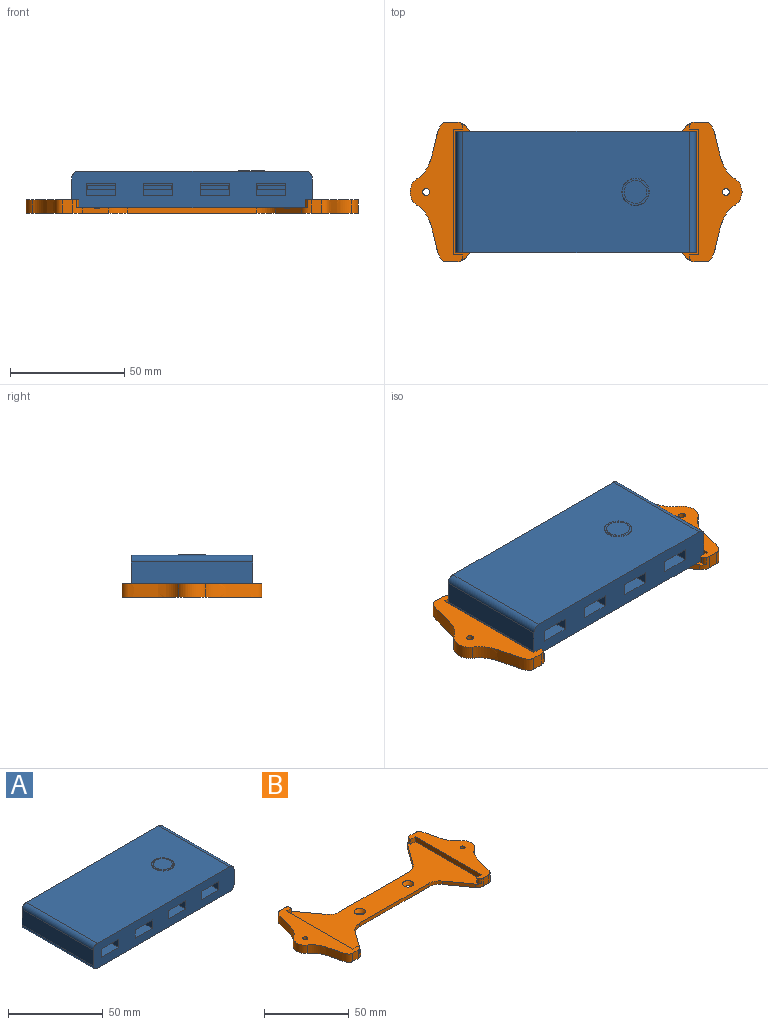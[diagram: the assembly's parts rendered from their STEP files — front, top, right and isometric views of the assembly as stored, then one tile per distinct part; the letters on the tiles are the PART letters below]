
ASSEMBLY  parts=2 mates=1
PART A: 89 faces, bbox 105x53x16.5 mm
  f0: plane 105x16mm, normal (0,1,0), area 1523.6mm2, adj f2,f3,f4,f5,f6,f7,f8,f9
  f1: plane 105x16mm, normal (0,-1,0), area 1399.4mm2, adj f2,f3,f4,f5,f6,f7,f8,f9
  f2: plane 53x10mm, normal (1,0,0), area 530mm2, adj f0,f1,f7,f9
  f3: plane 53x10mm, normal (-1,0,0), area 530mm2, adj f0,f1,f6,f8
  f4: plane 99x53mm, normal (0,0,1), area 5133.9mm2, adj f0,f1,f8,f9,f13
  f5: plane 99x53mm, normal (0,0,-1), area 5093.1mm2, adj f0,f1,f6,f7,f81,f83,f85,f87
  f6: cylinder r=3mm len=53mm, axis (0,-1,0), area 249.8mm2, adj f0,f1,f3,f5
  f7: cylinder r=3mm len=53mm, axis (0,1,0), area 249.8mm2, adj f0,f1,f2,f5
  f8: cylinder r=3mm len=53mm, axis (0,1,0), area 249.8mm2, adj f0,f1,f3,f4
  f9: cylinder r=3mm len=53mm, axis (0,-1,0), area 249.8mm2, adj f0,f1,f2,f4
  f10: plane 11.6x11.6mm, normal (0,0,1), area 27.1mm2, adj f11,f13
  f11: cylinder r=5mm len=10mm, axis (0,0,-1), area 1.6mm2, adj f10,f12
  f12: plane 10x10mm, normal (0,0,1), area 78.5mm2, adj f11
  f13: cone r=5.8mm half-angle=45deg, axis (0,0,-1), area 10.5mm2, adj f4,f10
  f14: plane 10x5.35mm, normal (-1,0,0), area 53.5mm2, adj f1,f15,f17,f49
  f15: plane 12.75x10mm, normal (0,0,-1), area 127.5mm2, adj f1,f14,f16,f49
  f16: plane 10x5.35mm, normal (1,0,0), area 53.5mm2, adj f1,f15,f17,f49
  f17: plane 12.75x10mm, normal (0,0,1), area 127.5mm2, adj f1,f14,f16,f49
  f18: plane 10x5.35mm, normal (-1,0,0), area 53.5mm2, adj f1,f19,f21,f44
  f19: plane 12.75x10mm, normal (0,0,-1), area 127.5mm2, adj f1,f18,f20,f44
  f20: plane 10x5.35mm, normal (1,0,0), area 53.5mm2, adj f1,f19,f21,f44
  f21: plane 12.75x10mm, normal (0,0,1), area 127.5mm2, adj f1,f18,f20,f44
  f22: plane 10x5.35mm, normal (-1,0,0), area 53.5mm2, adj f1,f23,f25,f39
  f23: plane 12.75x10mm, normal (0,0,-1), area 127.5mm2, adj f1,f22,f24,f39
  f24: plane 10x5.35mm, normal (1,0,0), area 53.5mm2, adj f1,f23,f25,f39
  f25: plane 12.75x10mm, normal (0,0,1), area 127.5mm2, adj f1,f22,f24,f39
  f26: plane 10x5.35mm, normal (-1,0,0), area 53.5mm2, adj f1,f27,f29,f34
  f27: plane 12.75x10mm, normal (0,0,-1), area 127.5mm2, adj f1,f26,f28,f34
  f28: plane 10x5.35mm, normal (1,0,0), area 53.5mm2, adj f1,f27,f29,f34
  f29: plane 12.75x10mm, normal (0,0,1), area 127.5mm2, adj f1,f26,f28,f34
  f30: plane 7.25x1.75mm, normal (-1,0,0), area 12.7mm2, adj f31,f33,f34,f50
  f31: plane 12.25x7.25mm, normal (0,0,1), area 88.8mm2, adj f30,f32,f34,f50
  f32: plane 7.25x1.75mm, normal (1,0,0), area 12.7mm2, adj f31,f33,f34,f50
  f33: plane 12.25x7.25mm, normal (0,0,-1), area 88.8mm2, adj f30,f32,f34,f50
  f34: plane 12.75x5.35mm, normal (0,-1,0), area 46.8mm2, adj f26,f27,f28,f29,f30,f31,f32,f33
  f35: plane 12.25x7.25mm, normal (0,0,-1), area 88.8mm2, adj f36,f38,f39,f51
  f36: plane 7.25x1.75mm, normal (-1,0,0), area 12.7mm2, adj f35,f37,f39,f51
  f37: plane 12.25x7.25mm, normal (0,0,1), area 88.8mm2, adj f36,f38,f39,f51
  f38: plane 7.25x1.75mm, normal (1,0,0), area 12.7mm2, adj f35,f37,f39,f51
  f39: plane 12.75x5.35mm, normal (0,-1,0), area 46.8mm2, adj f22,f23,f24,f25,f35,f36,f37,f38
  f40: plane 12.25x7.25mm, normal (0,0,-1), area 88.8mm2, adj f41,f43,f44,f52
  f41: plane 7.25x1.75mm, normal (-1,0,0), area 12.7mm2, adj f40,f42,f44,f52
  f42: plane 12.25x7.25mm, normal (0,0,1), area 88.8mm2, adj f41,f43,f44,f52
  f43: plane 7.25x1.75mm, normal (1,0,0), area 12.7mm2, adj f40,f42,f44,f52
  f44: plane 12.75x5.35mm, normal (0,-1,0), area 46.8mm2, adj f18,f19,f20,f21,f40,f41,f42,f43
  f45: plane 12.25x7.25mm, normal (0,0,-1), area 88.8mm2, adj f46,f48,f49,f53
  f46: plane 7.25x1.75mm, normal (-1,0,0), area 12.7mm2, adj f45,f47,f49,f53
  f47: plane 12.25x7.25mm, normal (0,0,1), area 88.8mm2, adj f46,f48,f49,f53
  f48: plane 7.25x1.75mm, normal (1,0,0), area 12.7mm2, adj f45,f47,f49,f53
  f49: plane 12.75x5.35mm, normal (0,-1,0), area 46.8mm2, adj f14,f15,f16,f17,f45,f46,f47,f48
  f50: plane 12.25x1.75mm, normal (0,-1,0), area 21.4mm2, adj f30,f31,f32,f33
  f51: plane 12.25x1.75mm, normal (0,-1,0), area 21.4mm2, adj f35,f36,f37,f38
  f52: plane 12.25x1.75mm, normal (0,-1,0), area 21.4mm2, adj f40,f41,f42,f43
  f53: plane 12.25x1.75mm, normal (0,-1,0), area 21.4mm2, adj f45,f46,f47,f48
  f54: plane 12.75x10.25mm, normal (0,0,-1), area 130.7mm2, adj f0,f55,f57,f71
  f55: plane 10.25x5.35mm, normal (-1,0,0), area 54.8mm2, adj f0,f54,f56,f71
  f56: plane 12.75x10.25mm, normal (0,0,1), area 130.7mm2, adj f0,f55,f57,f71
  f57: plane 10.25x5.35mm, normal (1,0,0), area 54.8mm2, adj f0,f54,f56,f71
  f58: plane 10.25x5.35mm, normal (1,0,0), area 54.8mm2, adj f0,f59,f61,f66
  f59: plane 12.75x10.25mm, normal (0,0,-1), area 130.7mm2, adj f0,f58,f60,f66
  f60: plane 10.25x5.35mm, normal (-1,0,0), area 54.8mm2, adj f0,f59,f61,f66
  f61: plane 12.75x10.25mm, normal (0,0,1), area 130.7mm2, adj f0,f58,f60,f66
  f62: plane 7.75x1.75mm, normal (1,0,0), area 13.6mm2, adj f63,f65,f66,f72
  f63: plane 12.25x7.75mm, normal (0,0,1), area 94.9mm2, adj f62,f64,f66,f72
  f64: plane 7.75x1.75mm, normal (-1,0,0), area 13.6mm2, adj f63,f65,f66,f72
  f65: plane 12.25x7.75mm, normal (0,0,-1), area 94.9mm2, adj f62,f64,f66,f72
  f66: plane 12.75x5.35mm, normal (0,1,0), area 46.8mm2, adj f58,f59,f60,f61,f62,f63,f64,f65
  f67: plane 7.75x1.75mm, normal (1,0,0), area 13.6mm2, adj f68,f70,f71,f73
  f68: plane 12.25x7.75mm, normal (0,0,1), area 94.9mm2, adj f67,f69,f71,f73
  f69: plane 7.75x1.75mm, normal (-1,0,0), area 13.6mm2, adj f68,f70,f71,f73
  f70: plane 12.25x7.75mm, normal (0,0,-1), area 94.9mm2, adj f67,f69,f71,f73
  f71: plane 12.75x5.35mm, normal (0,1,0), area 46.8mm2, adj f54,f55,f56,f57,f67,f68,f69,f70
  f72: plane 12.25x1.75mm, normal (0,1,0), area 21.4mm2, adj f62,f63,f64,f65
  f73: plane 12.25x1.75mm, normal (0,1,0), area 21.4mm2, adj f67,f68,f69,f70
  f74: plane 6.9x4mm, normal (0,0,-1), area 27.6mm2, adj f0,f75,f79,f80
  f75: plane 4x1.1mm, normal (-1,0,0), area 4.4mm2, adj f0,f74,f76,f80
  f76: plane 4x0.75mm, normal (-0.73,0,0.68), area 4.1mm2, adj f0,f75,f77,f80
  f77: plane 5.5x4mm, normal (0,0,1), area 22mm2, adj f0,f76,f78,f80
  f78: plane 4x0.75mm, normal (0.73,0,0.68), area 4.1mm2, adj f0,f77,f79,f80
  f79: plane 4x1.1mm, normal (1,0,0), area 4.4mm2, adj f0,f74,f78,f80
  f80: plane 6.9x1.85mm, normal (0,1,0), area 12.2mm2, adj f74,f75,f76,f77,f78,f79
  f81: cylinder r=3.5mm len=7mm, axis (0,0,1), area 5.5mm2, adj f5,f82
  f82: plane 7x7mm, normal (0,0,-1), area 38.5mm2, adj f81
  f83: cylinder r=3.5mm len=7mm, axis (0,0,1), area 5.5mm2, adj f5,f84
  f84: plane 7x7mm, normal (0,0,-1), area 38.5mm2, adj f83
  f85: cylinder r=3.5mm len=7mm, axis (0,0,1), area 5.5mm2, adj f5,f86
  f86: plane 7x7mm, normal (0,0,-1), area 38.5mm2, adj f85
  f87: cylinder r=3.5mm len=7mm, axis (0,0,1), area 5.5mm2, adj f5,f88
  f88: plane 7x7mm, normal (0,0,-1), area 38.5mm2, adj f87
PART B: 60 faces, bbox 145x61x6 mm
  f0: plane 145x61mm, normal (0,0,-1), area 4109.9mm2, adj f2,f3,f8,f9,f10,f11,f12,f13
  f1: plane 107x60.55mm, normal (0,0,1), area 2740.6mm2, adj f5,f6,f16,f17,f18,f19,f20,f21
  f2: plane 6x4.44mm, normal (0,1,0), area 26.6mm2, adj f0,f7,f15,f56
  f3: plane 6x4.44mm, normal (0,-1,0), area 26.6mm2, adj f0,f7,f12,f59
  f4: plane 61x23mm, normal (0,0,1), area 678.7mm2, adj f5,f6,f8,f9,f10,f11,f14,f19
  f5: plane 4x3.5mm, normal (0,-1,0), area 14mm2, adj f1,f4,f19,f23
  f6: plane 4x3.5mm, normal (0,1,0), area 14mm2, adj f1,f4,f19,f21
  f7: plane 61x23mm, normal (0,0,1), area 678.7mm2, adj f2,f3,f12,f13,f15,f16,f17,f18
  f8: plane 6x4.44mm, normal (0,1,0), area 26.6mm2, adj f0,f4,f14,f57
  f9: plane 6x4.44mm, normal (0,-1,0), area 26.6mm2, adj f0,f4,f11,f58
  f10: cylinder r=7.07mm len=11.45mm, axis (0,0,1), area 80mm2, adj f0,f4,f11,f14
  f11: extruded ~24.78x13.08mm, area 176.1mm2, adj f0,f4,f9,f10
  f12: extruded ~24.78x13.08mm, area 176.1mm2, adj f0,f3,f7,f13
  f13: cylinder r=7.07mm len=11.45mm, axis (0,0,1), area 80mm2, adj f0,f7,f12,f15
  f14: extruded ~24.78x13.08mm, area 176.1mm2, adj f0,f4,f8,f10
  f15: extruded ~24.78x13.08mm, area 176.1mm2, adj f0,f2,f7,f13
  f16: plane 55x3.5mm, normal (1,0,0), area 192.5mm2, adj f1,f7,f17,f18
  f17: plane 4x3.5mm, normal (0,-1,0), area 14mm2, adj f1,f7,f16,f22
  f18: plane 4x3.5mm, normal (0,1,0), area 14mm2, adj f1,f7,f16,f20
  f19: plane 55x3.5mm, normal (-1,0,0), area 192.5mm2, adj f1,f4,f5,f6
  f20: plane 3.5x1mm, normal (1,0,0), area 3.5mm2, adj f1,f7,f18,f54
  f21: plane 3.5x1mm, normal (-1,0,0), area 3.5mm2, adj f1,f4,f6,f55
  f22: plane 3.5x1mm, normal (1,0,0), area 3.5mm2, adj f1,f7,f17,f52
  f23: plane 3.5x1mm, normal (-1,0,0), area 3.5mm2, adj f1,f4,f5,f53
  f24: plane 15.97x11.51mm, normal (0.81,0.58,0), area 49.2mm2, adj f0,f1,f26,f56
  f25: plane 15.97x11.51mm, normal (-0.81,0.58,0), area 49.2mm2, adj f0,f1,f28,f57
  f26: cylinder r=10mm len=8.11mm, axis (0,0,1), area 23.7mm2, adj f0,f1,f24,f27
  f27: plane 56.76x2.5mm, normal (0,1,0), area 141.9mm2, adj f0,f1,f26,f28
  f28: cylinder r=10mm len=8.11mm, axis (0,0,1), area 23.7mm2, adj f0,f1,f25,f27
  f29: plane 15.97x11.51mm, normal (-0.81,-0.58,0), area 49.2mm2, adj f0,f1,f31,f58
  f30: plane 15.97x11.51mm, normal (0.81,-0.58,0), area 49.2mm2, adj f0,f1,f33,f59
  f31: cylinder r=10mm len=8.11mm, axis (0,0,1), area 23.7mm2, adj f0,f1,f29,f32
  f32: plane 56.76x2.5mm, normal (0,-1,0), area 141.9mm2, adj f0,f1,f31,f33
  f33: cylinder r=10mm len=8.11mm, axis (0,0,1), area 23.7mm2, adj f0,f1,f30,f32
  f34: cone r=3.3mm half-angle=30deg, axis (0,0,1), area 46.8mm2, adj f0,f1
  f35: cone r=3.3mm half-angle=30deg, axis (0,0,1), area 46.8mm2, adj f0,f1
  f36: cylinder r=1.5mm len=3.25mm, axis (0,0,1), area 30.6mm2, adj f4,f51
  f37: cylinder r=1.5mm len=3.25mm, axis (0,0,1), area 30.6mm2, adj f7,f44
  f38: plane 2.75x2.53mm, normal (0.57,0.82,0), area 8.5mm2, adj f0,f39,f43,f44
  f39: plane 2.78x2.75mm, normal (-0.43,0.9,0), area 8.5mm2, adj f0,f38,f40,f44
  f40: plane 3.06x2.75mm, normal (-1,0.08,0), area 8.5mm2, adj f0,f39,f41,f44
  f41: plane 2.75x2.53mm, normal (-0.57,-0.82,0), area 8.5mm2, adj f0,f40,f42,f44
  f42: plane 2.78x2.75mm, normal (0.43,-0.9,0), area 8.5mm2, adj f0,f41,f43,f44
  f43: plane 3.06x2.75mm, normal (1,-0.08,0), area 8.5mm2, adj f0,f38,f42,f44
  f44: plane 6.13x5.56mm, normal (0,0,-1), area 17.5mm2, adj f37,f38,f39,f40,f41,f42,f43
  f45: plane 3.06x2.75mm, normal (1,0.08,0), area 8.5mm2, adj f0,f46,f50,f51
  f46: plane 2.78x2.75mm, normal (0.43,0.9,0), area 8.5mm2, adj f0,f45,f47,f51
  f47: plane 2.75x2.53mm, normal (-0.57,0.82,0), area 8.5mm2, adj f0,f46,f48,f51
  f48: plane 3.06x2.75mm, normal (-1,-0.08,0), area 8.5mm2, adj f0,f47,f49,f51
  f49: plane 2.78x2.75mm, normal (-0.43,-0.9,0), area 8.5mm2, adj f0,f48,f50,f51
  f50: plane 2.75x2.53mm, normal (0.57,-0.82,0), area 8.5mm2, adj f0,f45,f49,f51
  f51: plane 6.13x5.56mm, normal (0,0,-1), area 17.5mm2, adj f36,f45,f46,f47,f48,f49,f50
  f52: cylinder r=2mm len=3.5mm, axis (0,0,-1), area 7.7mm2, adj f1,f7,f22,f56
  f53: cylinder r=2mm len=3.5mm, axis (0,0,1), area 7.7mm2, adj f1,f4,f23,f57
  f54: cylinder r=2mm len=3.5mm, axis (0,0,1), area 7.7mm2, adj f1,f7,f20,f59
  f55: cylinder r=2mm len=3.5mm, axis (0,0,-1), area 7.7mm2, adj f1,f4,f21,f58
  f56: cylinder r=5mm len=6mm, axis (0,0,1), area 17.1mm2, adj f0,f1,f2,f7,f24,f52
  f57: cylinder r=5mm len=6mm, axis (0,0,1), area 17.1mm2, adj f0,f1,f4,f8,f25,f53
  f58: cylinder r=5mm len=6mm, axis (0,0,1), area 17.1mm2, adj f0,f1,f4,f9,f29,f55
  f59: cylinder r=5mm len=6mm, axis (0,0,-1), area 17.1mm2, adj f0,f1,f3,f7,f30,f54
PLACE A t=(26.83,1.8,36.03)mm
PLACE B t=(26.83,1.8,33.53)mm fixed
MATE slider A.f5 <-> B.f1  axis (0,0,-1) through (26.83,1.8,36.03)mm
